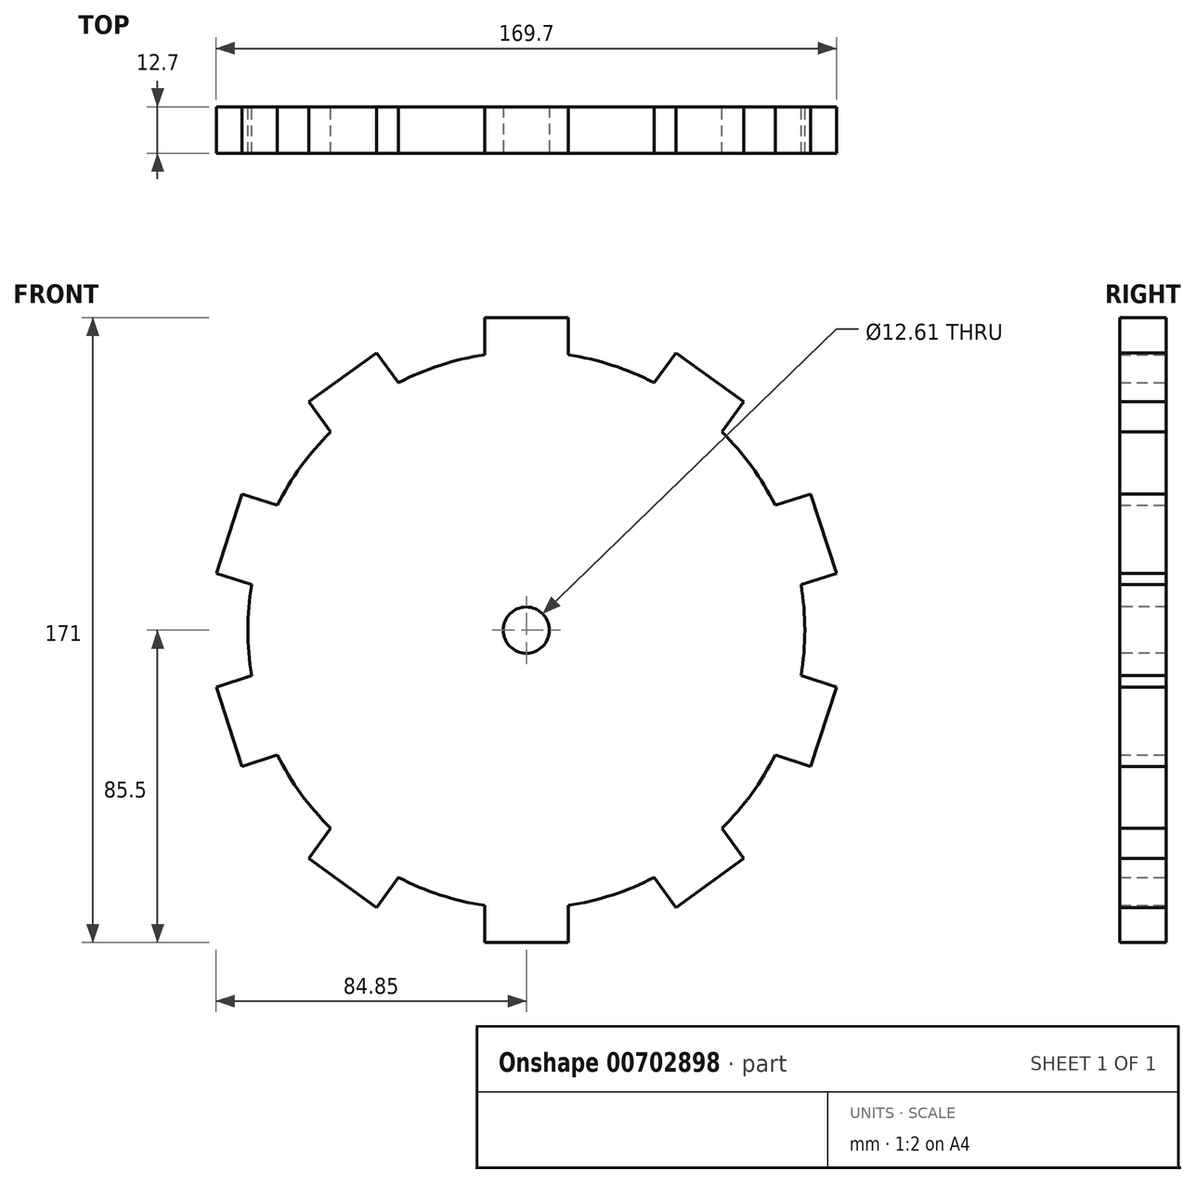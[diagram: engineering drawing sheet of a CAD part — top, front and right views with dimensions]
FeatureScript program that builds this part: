
annotation { "Feature Type Name" : "Feature", "Feature Type Description" : "" }
export const myFeature = defineFeature(function(context is Context, id is Id, definition is map)
    precondition{}
    {
        {
            var Q0;
            Q0=qCreatedBy(makeId("Front.planeOp"),FACE);
            var sketch = newSketch(context, id + "F0", { "sketchPlane" : qUnion([Q0])});
            skCircle(sketch, "E0", {"center": v(0, 0) * mm, "radius": 76.2 * mm});
            skLineSegment(sketch, "E1.bottom", {"start": v(11.43, 75.34) * mm, "end": v(-11.43, 75.34) * mm});
            skLineSegment(sketch, "E1.top", {"start": v(11.43, 85.5) * mm, "end": v(-11.43, 85.5) * mm});
            skLineSegment(sketch, "E1.left", {"start": v(11.43, 75.34) * mm, "end": v(11.43, 85.5) * mm});
            skLineSegment(sketch, "E1.right", {"start": v(-11.43, 75.34) * mm, "end": v(-11.43, 85.5) * mm});
            skPoint(sketch, "E1.middle", {"position": v(0, 80.42) * mm});
            skLineSegment(sketch, "E2.1.0", {"start": v(-41, 75.89) * mm, "end": v(-59.5, 62.45) * mm});
            skLineSegment(sketch, "E2.1.1", {"start": v(-35.04, 67.67) * mm, "end": v(-41, 75.89) * mm});
            skLineSegment(sketch, "E2.1.2", {"start": v(-53.53, 54.23) * mm, "end": v(-59.5, 62.45) * mm});
            skLineSegment(sketch, "E2.2.0", {"start": v(-77.78, 37.3) * mm, "end": v(-84.85, 15.55) * mm});
            skLineSegment(sketch, "E2.2.1", {"start": v(-68.12, 34.15) * mm, "end": v(-77.78, 37.3) * mm});
            skLineSegment(sketch, "E2.2.2", {"start": v(-75.18, 12.41) * mm, "end": v(-84.85, 15.55) * mm});
            skLineSegment(sketch, "E2.3.0", {"start": v(-84.85, -15.55) * mm, "end": v(-77.78, -37.3) * mm});
            skLineSegment(sketch, "E2.3.1", {"start": v(-75.18, -12.41) * mm, "end": v(-84.85, -15.55) * mm});
            skLineSegment(sketch, "E2.3.2", {"start": v(-68.12, -34.15) * mm, "end": v(-77.78, -37.3) * mm});
            skLineSegment(sketch, "E2.4.0", {"start": v(-59.5, -62.45) * mm, "end": v(-41, -75.89) * mm});
            skLineSegment(sketch, "E2.4.1", {"start": v(-53.53, -54.23) * mm, "end": v(-59.5, -62.45) * mm});
            skLineSegment(sketch, "E2.4.2", {"start": v(-35.04, -67.67) * mm, "end": v(-41, -75.89) * mm});
            skLineSegment(sketch, "E2.5.0", {"start": v(-11.43, -85.5) * mm, "end": v(11.43, -85.5) * mm});
            skLineSegment(sketch, "E2.5.1", {"start": v(-11.43, -75.34) * mm, "end": v(-11.43, -85.5) * mm});
            skLineSegment(sketch, "E2.5.2", {"start": v(11.43, -75.34) * mm, "end": v(11.43, -85.5) * mm});
            skLineSegment(sketch, "E2.6.0", {"start": v(41, -75.89) * mm, "end": v(59.5, -62.45) * mm});
            skLineSegment(sketch, "E2.6.1", {"start": v(35.04, -67.67) * mm, "end": v(41, -75.89) * mm});
            skLineSegment(sketch, "E2.6.2", {"start": v(53.53, -54.23) * mm, "end": v(59.5, -62.45) * mm});
            skLineSegment(sketch, "E2.7.0", {"start": v(77.78, -37.3) * mm, "end": v(84.85, -15.55) * mm});
            skLineSegment(sketch, "E2.7.1", {"start": v(68.12, -34.15) * mm, "end": v(77.78, -37.3) * mm});
            skLineSegment(sketch, "E2.7.2", {"start": v(75.18, -12.41) * mm, "end": v(84.85, -15.55) * mm});
            skLineSegment(sketch, "E2.8.0", {"start": v(84.85, 15.55) * mm, "end": v(77.78, 37.3) * mm});
            skLineSegment(sketch, "E2.8.1", {"start": v(75.18, 12.41) * mm, "end": v(84.85, 15.55) * mm});
            skLineSegment(sketch, "E2.8.2", {"start": v(68.12, 34.15) * mm, "end": v(77.78, 37.3) * mm});
            skLineSegment(sketch, "E2.9.0", {"start": v(59.5, 62.45) * mm, "end": v(41, 75.89) * mm});
            skLineSegment(sketch, "E2.9.1", {"start": v(53.53, 54.23) * mm, "end": v(59.5, 62.45) * mm});
            skLineSegment(sketch, "E2.9.2", {"start": v(35.04, 67.67) * mm, "end": v(41, 75.89) * mm});
            skSolve(sketch);
        }
        {
            var Q0;
            Q0 = qSketchRegion(id + "F0", true);
            extrude(context, id + "F1", {"entities" : qUnion([Q0]), "depth" : 12.7 * mm, "offsetDistance" : 25.4 * mm});
        }
        {
            var Q0;
            Q0=makeQuery(id+"F1.opExtrude","CAP_FACE",FACE,{"disambiguationData":[OSD([sQuery(id+"F0.wireOp",EDGE,"E0"),sQuery(id+"F0.wireOp",EDGE,"E1.top"),sQuery(id+"F0.wireOp",EDGE,"E1.left"),sQuery(id+"F0.wireOp",EDGE,"E1.right"),sQuery(id+"F0.wireOp",EDGE,"E2.1.0"),sQuery(id+"F0.wireOp",EDGE,"E2.1.1"),sQuery(id+"F0.wireOp",EDGE,"E2.1.2"),sQuery(id+"F0.wireOp",EDGE,"E2.2.0"),sQuery(id+"F0.wireOp",EDGE,"E2.2.1"),sQuery(id+"F0.wireOp",EDGE,"E2.2.2"),sQuery(id+"F0.wireOp",EDGE,"E2.3.0"),sQuery(id+"F0.wireOp",EDGE,"E2.3.1"),sQuery(id+"F0.wireOp",EDGE,"E2.3.2"),sQuery(id+"F0.wireOp",EDGE,"E2.4.0"),sQuery(id+"F0.wireOp",EDGE,"E2.4.1"),sQuery(id+"F0.wireOp",EDGE,"E2.4.2"),sQuery(id+"F0.wireOp",EDGE,"E2.5.0"),sQuery(id+"F0.wireOp",EDGE,"E2.5.1"),sQuery(id+"F0.wireOp",EDGE,"E2.5.2"),sQuery(id+"F0.wireOp",EDGE,"E2.6.0"),sQuery(id+"F0.wireOp",EDGE,"E2.6.1"),sQuery(id+"F0.wireOp",EDGE,"E2.6.2"),sQuery(id+"F0.wireOp",EDGE,"E2.7.0"),sQuery(id+"F0.wireOp",EDGE,"E2.7.1"),sQuery(id+"F0.wireOp",EDGE,"E2.7.2"),sQuery(id+"F0.wireOp",EDGE,"E2.8.0"),sQuery(id+"F0.wireOp",EDGE,"E2.8.1"),sQuery(id+"F0.wireOp",EDGE,"E2.8.2"),sQuery(id+"F0.wireOp",EDGE,"E2.9.0"),sQuery(id+"F0.wireOp",EDGE,"E2.9.1"),sQuery(id+"F0.wireOp",EDGE,"E2.9.2")])],"isStart":false});
            var sketch = newSketch(context, id + "F2", { "sketchPlane" : qUnion([Q0])});
            skCircle(sketch, "E3", {"center": v(0, 0) * mm, "radius": 6.3 * mm});
            skSolve(sketch);
        }
        {
            var Q0;
            Q0 = qSketchRegion(id + "F2", true);
            extrude(context, id + "F3", {"entities" : qUnion([Q0]), "operationType" : NewBodyOperationType.REMOVE, "oppositeDirection" : true, "depth" : 12.7 * mm, "offsetDistance" : 25.4 * mm});
        }
    });
